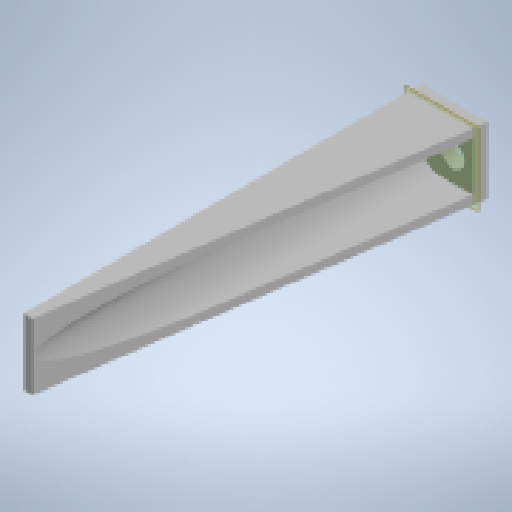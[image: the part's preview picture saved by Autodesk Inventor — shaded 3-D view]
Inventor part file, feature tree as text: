
AUTODESK INVENTOR PART (.ipt)
format: ipt  version: 2023 (Build 270158000, 158)  size: 159,232 bytes
history: native  units: mm
features: extrude x3, sketch x3, plane x1, fillet x1
ambient origin geometry x8: Origin, YZ Plane, XZ Plane, XY Plane, X Axis, Y Axis, Z Axis, Center Point
bodies: Solid1 (feature_tree)
feature tree (8):
  extrude  "Extrusion1"  Depth=17.5mm
  plane  "Work Plane1"
  extrude  "Extrusion2"  Depth=15.0mm TaperAngle=0.0deg
  extrude  "Extrusion3"  [1 undecoded]
  fillet  "Fillet1"  Radius=15.0mm
  sketch  "Sketch1"  dims[d0=90.0mm d1=17.5mm]
  sketch  "Sketch2"  dims[d2=2.0mm d3=15.0mm d4=0.0mm]
  sketch  "Sketch3"  dims[d5=2.0mm d6=-3.0mm d7=15.0mm d8=0.0mm d9=5.226mm d10=5.0mm d11=10.0mm d12=0.0mm d13=2.0mm]
note: 1 required parameter value undecoded (feature->parameter linkage not recoverable at this tier; creation-order binding heuristic only, values carry confidence <= 0.55)
